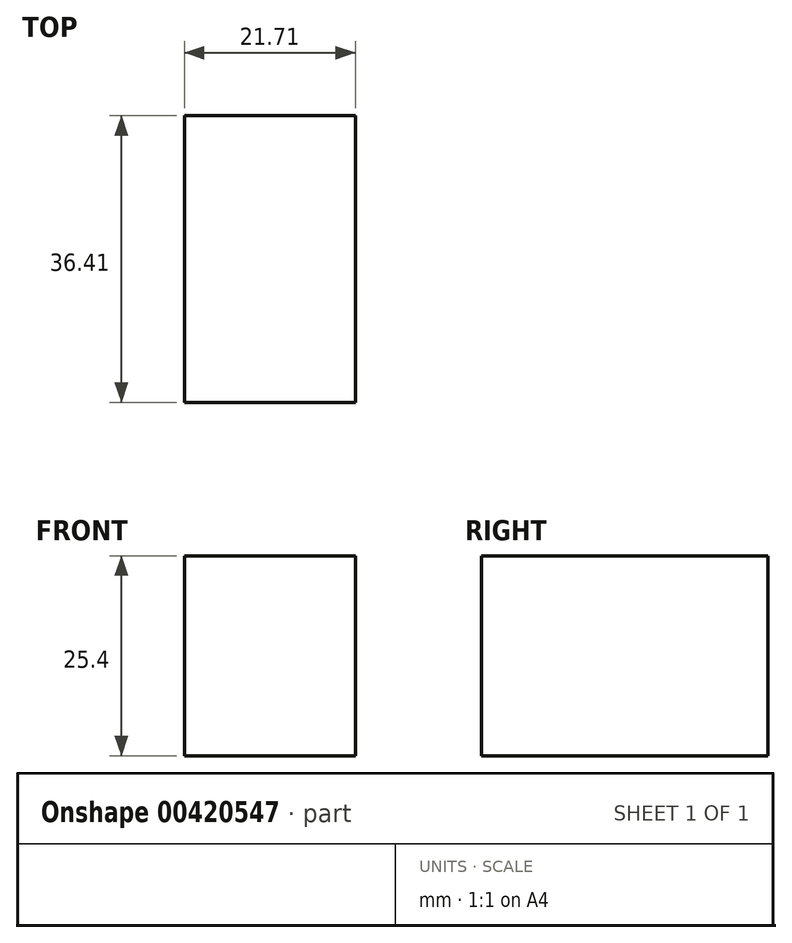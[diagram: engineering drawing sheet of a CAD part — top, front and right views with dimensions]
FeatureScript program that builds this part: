
annotation { "Feature Type Name" : "Feature", "Feature Type Description" : "" }
export const myFeature = defineFeature(function(context is Context, id is Id, definition is map)
    precondition{}
    {
        {
            var Q0;
            Q0=qCreatedBy(makeId("Top.planeOp"),FACE);
            var sketch = newSketch(context, id + "F0", { "sketchPlane" : qUnion([Q0])});
            skLineSegment(sketch, "E0.bottom", {"start": v(24.78, -15.77) * mm, "end": v(46.5, -15.77) * mm});
            skLineSegment(sketch, "E0.top", {"start": v(24.78, -52.18) * mm, "end": v(46.5, -52.18) * mm});
            skLineSegment(sketch, "E0.left", {"start": v(24.78, -15.77) * mm, "end": v(24.78, -52.18) * mm});
            skLineSegment(sketch, "E0.right", {"start": v(46.5, -15.77) * mm, "end": v(46.5, -52.18) * mm});
            skSolve(sketch);
        }
        {
            var Q0;
            Q0=makeQuery(id+"F0.imprint","IMPRINT",FACE,{"disambiguationData":[TD([[makeQuery(id+"F0.imprint","IMPRINT",EDGE,{"derivedFrom":sQuery(id+"F0.wireOp",EDGE,"E0.bottom")}),-1.0]])]});
            extrude(context, id + "F1", {"entities" : qUnion([Q0]), "depth" : 25.4 * mm});
        }
    });
